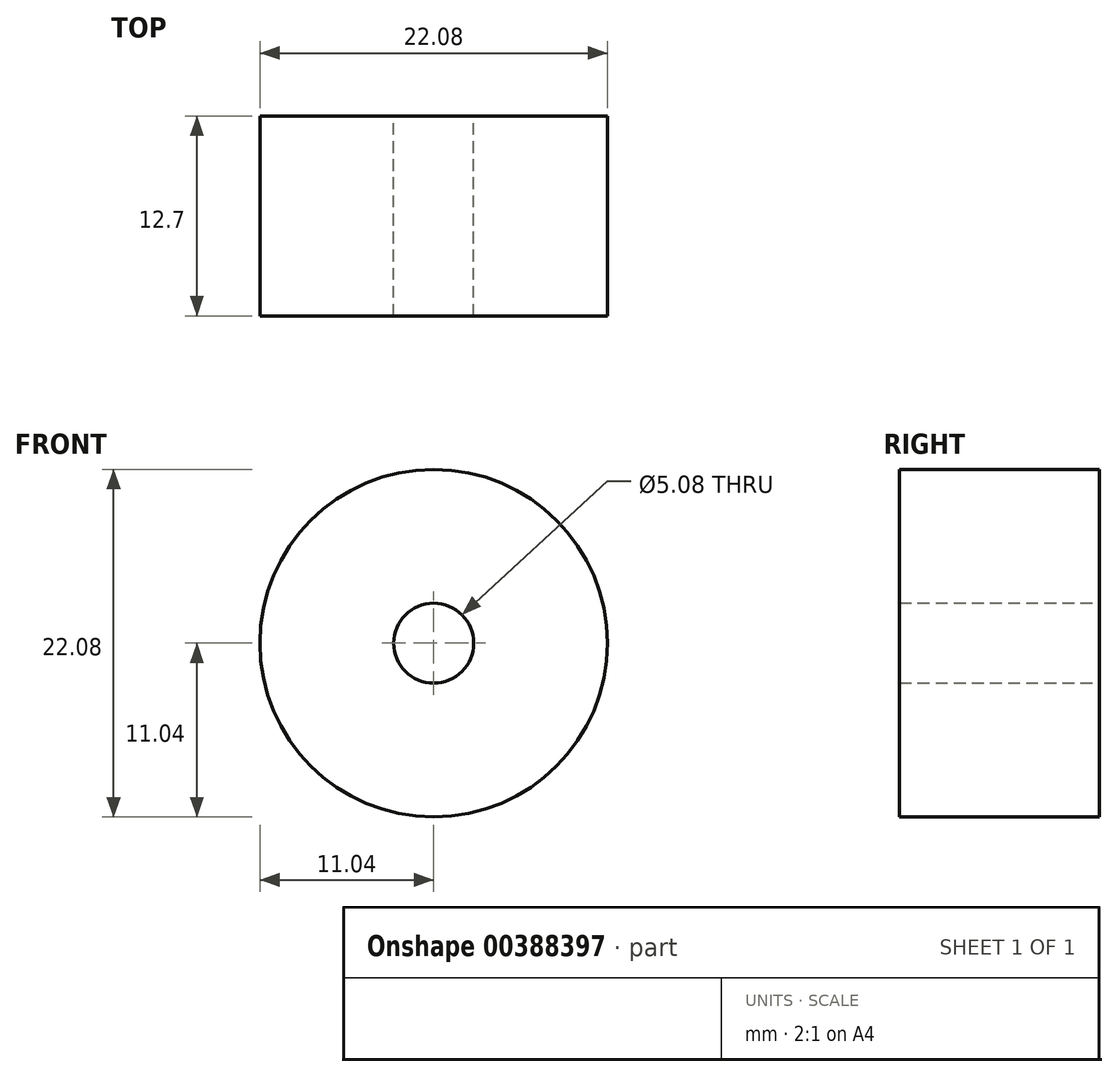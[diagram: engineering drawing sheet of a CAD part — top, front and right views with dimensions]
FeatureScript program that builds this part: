
annotation { "Feature Type Name" : "Feature", "Feature Type Description" : "" }
export const myFeature = defineFeature(function(context is Context, id is Id, definition is map)
    precondition{}
    {
        {
            var Q0;
            Q0=qCreatedBy(makeId("Front.planeOp"),FACE);
            var sketch = newSketch(context, id + "F0", { "sketchPlane" : qUnion([Q0])});
            skCircle(sketch, "E0", {"center": v(0, 0) * mm, "radius": 11.04 * mm});
            skCircle(sketch, "E1", {"center": v(0, 0) * mm, "radius": 2.54 * mm});
            skSolve(sketch);
        }
        {
            var Q0;
            Q0 = qSketchRegion(id + "F0", true);
            extrude(context, id + "F1", {"entities" : qUnion([Q0]), "depth" : 12.7 * mm});
        }
    });
